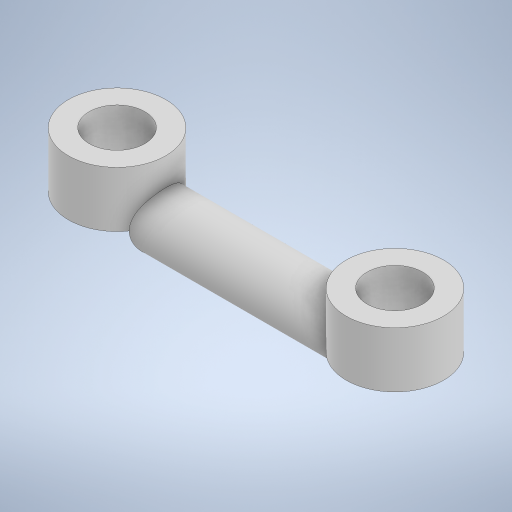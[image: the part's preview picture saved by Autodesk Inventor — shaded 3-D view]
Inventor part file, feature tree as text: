
AUTODESK INVENTOR PART (.ipt)
format: ipt  version: 2024 (Build 280153000, 153)  size: 277,504 bytes
history: native  units: in
note: dims shown in document units (in); Inventor stores cm internally (conversion verified against a paired STEP export)
features: extrude x6, sketch x3, revolve x1
ambient origin geometry x8: Origin, YZ Plane, XZ Plane, XY Plane, X Axis, Y Axis, Z Axis, Center Point
bodies: Solid1 (feature_tree)
feature tree (10):
  revolve  "Revolution1"  [1 undecoded]
  sketch  "Sketch2"  dims[d2=90.0deg d3=1.378in]
  extrude  "Extrusion1"  Depth=1.378in
  extrude  "Extrusion2"  Depth=0.7874in TaperAngle=0.0deg
  extrude  "Extrusion3"  Depth=0.7874in TaperAngle=0.0deg
  sketch  "Sketch4"  dims[d4=0.7874in d5=0.7874in d6=0.0in d7=0.7874in d8=0.0in d9=0.7874in d10=0.0in d17=1.378in d18=0.7874in d19=0.7874in d20=0.0in d21=0.7874in d22=0.0in d23=0.7874in d24=0.0in]
  extrude  "Extrusion6"  Depth=0.7874in TaperAngle=0.0deg
  extrude  "Extrusion7"  Depth=1.378in
  extrude  "Extrusion8"  Depth=0.7874in
  sketch  "Sketch1"  dims[d0=3.937in d1=0.3937in]
note: 1 required parameter value undecoded (feature->parameter linkage not recoverable at this tier; creation-order binding heuristic only, values carry confidence <= 0.55)
